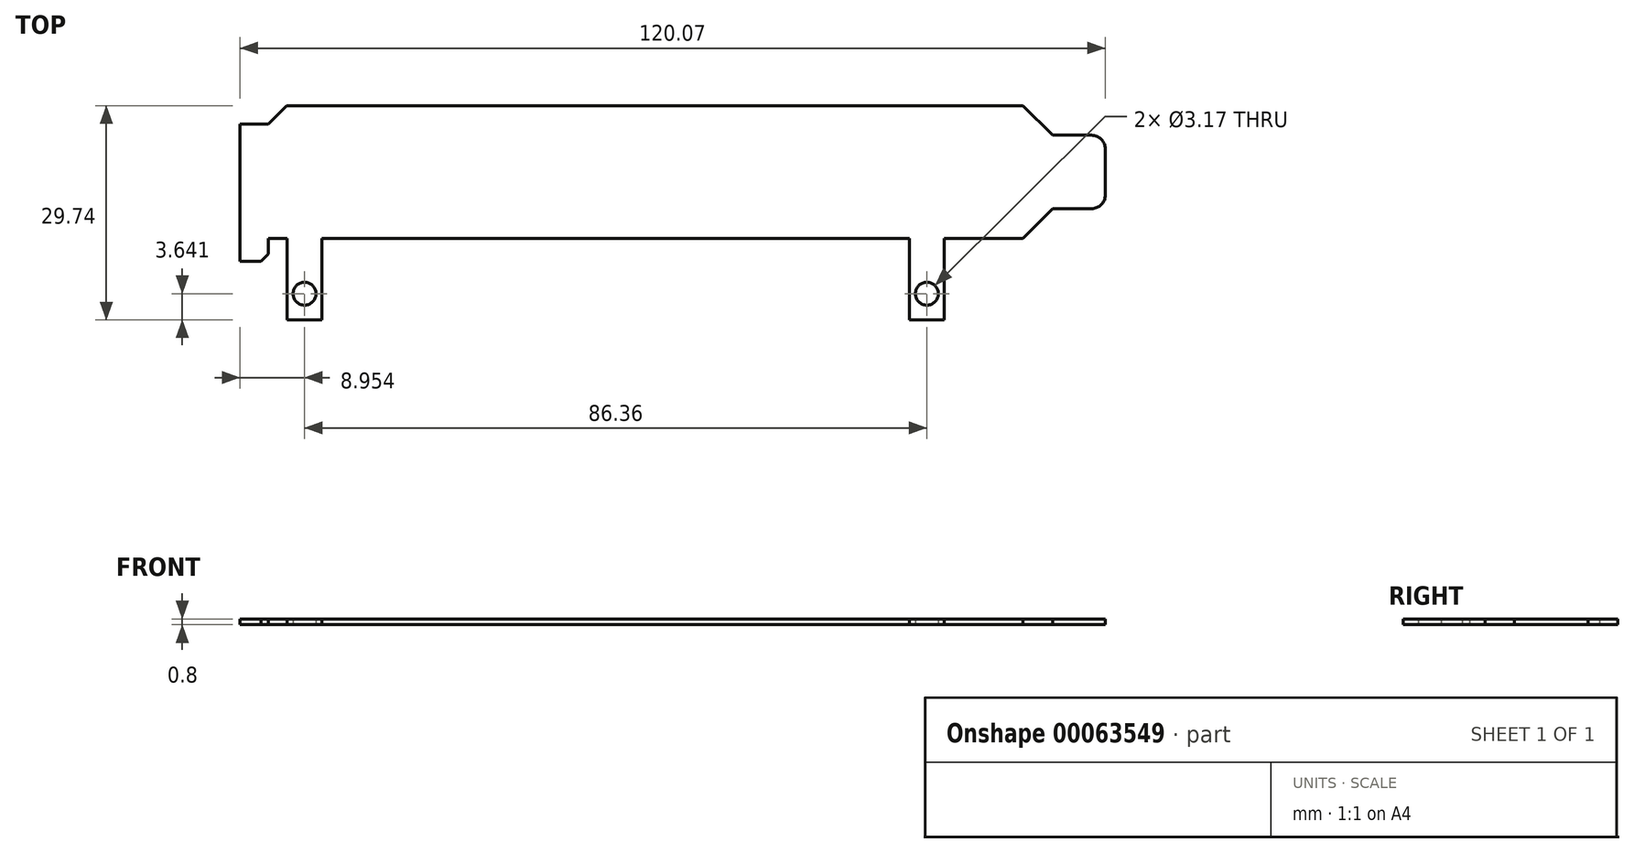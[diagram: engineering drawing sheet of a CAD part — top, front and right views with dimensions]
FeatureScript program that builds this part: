
annotation { "Feature Type Name" : "Feature", "Feature Type Description" : "" }
export const myFeature = defineFeature(function(context is Context, id is Id, definition is map)
    precondition{}
    {
        {
            var Q0;
            Q0=qCreatedBy(makeId("Top.planeOp"),FACE);
            var sketch = newSketch(context, id + "F0", { "sketchPlane" : qUnion([Q0])});
            skLineSegment(sketch, "E0.bottom", {"start": v(0, 0) * mm, "end": v(120.02, 0) * mm, "construction": true});
            skLineSegment(sketch, "E0.top", {"start": v(0, -18.41) * mm, "end": v(120.02, -18.41) * mm, "construction": true});
            skLineSegment(sketch, "E0.left", {"start": v(0, 0) * mm, "end": v(0, -18.41) * mm, "construction": true});
            skLineSegment(sketch, "E1.bottom", {"start": v(118.16, -4.11) * mm, "end": v(112.75, -4.11) * mm});
            skLineSegment(sketch, "E1.top", {"start": v(118.16, -14.3) * mm, "end": v(112.75, -14.3) * mm});
            skLineSegment(sketch, "E1.left", {"start": v(120.07, -6.02) * mm, "end": v(120.07, -12.4) * mm});
            skLineSegment(sketch, "E2", {"start": v(112.75, -4.11) * mm, "end": v(108.64, 0) * mm});
            skLineSegment(sketch, "E3", {"start": v(112.75, -14.3) * mm, "end": v(108.64, -18.41) * mm});
            skPoint(sketch, "E4.visualSharp", {"position": v(120.07, -4.11) * mm});
            skArc(sketch, "E4.filletArc", {"start": v(120.07, -6.02) * mm, "mid": v(119.5, -4.67) * mm, "end": v(118.16, -4.11) * mm});
            skPoint(sketch, "E5.visualSharp", {"position": v(120.07, -14.3) * mm});
            skArc(sketch, "E5.filletArc", {"start": v(118.16, -14.3) * mm, "mid": v(119.5, -13.74) * mm, "end": v(120.07, -12.4) * mm});
            skLineSegment(sketch, "E6", {"start": v(0, -2.54) * mm, "end": v(3.94, -2.54) * mm});
            skLineSegment(sketch, "E7", {"start": v(3.94, -2.54) * mm, "end": v(6.48, 0) * mm});
            skLineSegment(sketch, "E8", {"start": v(0, -18.41) * mm, "end": v(0, -21.59) * mm});
            skLineSegment(sketch, "E9", {"start": v(0, -21.59) * mm, "end": v(2.92, -21.59) * mm});
            skLineSegment(sketch, "E10", {"start": v(2.92, -21.59) * mm, "end": v(3.94, -20.57) * mm});
            skLineSegment(sketch, "E11", {"start": v(3.94, -20.57) * mm, "end": v(3.94, -18.41) * mm});
            skLineSegment(sketch, "E12", {"start": v(6.48, 0) * mm, "end": v(108.64, 0) * mm});
            skLineSegment(sketch, "E13", {"start": v(3.94, -18.41) * mm, "end": v(108.64, -18.41) * mm});
            skLineSegment(sketch, "E14", {"start": v(0, -2.54) * mm, "end": v(0, -18.41) * mm});
            skLineSegment(sketch, "E15", {"start": v(120.02, 0) * mm, "end": v(100.2, 0) * mm, "construction": true});
            skLineSegment(sketch, "E16", {"start": v(120.02, 24.3) * mm, "end": v(100.2, 24.3) * mm, "construction": true});
            skLineSegment(sketch, "E17", {"start": v(100.2, 24.3) * mm, "end": v(96.9, 24.3) * mm, "construction": true});
            skLineSegment(sketch, "E18", {"start": v(96.9, 24.3) * mm, "end": v(93.73, 24.3) * mm, "construction": true});
            skPoint(sketch, "E19.endSnap0", {"position": v(110.1, 0) * mm});
            skPoint(sketch, "E20", {"position": v(95.31, 24.3) * mm});
            skCircle(sketch, "E21", {"center": v(95.31, -26.1) * mm, "radius": 1.59 * mm});
            skLineSegment(sketch, "E22.top", {"start": v(92.91, -29.74) * mm, "end": v(97.71, -29.74) * mm});
            skLineSegment(sketch, "E22.left", {"start": v(92.91, -29.74) * mm, "end": v(92.91, -18.41) * mm});
            skLineSegment(sketch, "E22.right", {"start": v(97.71, -29.74) * mm, "end": v(97.71, -18.41) * mm});
            skPoint(sketch, "E23", {"position": v(95.31, -29.74) * mm});
            skCircle(sketch, "E24.1.0.0", {"center": v(8.95, -26.1) * mm, "radius": 1.59 * mm});
            skLineSegment(sketch, "E24.1.0.1", {"start": v(6.55, -29.74) * mm, "end": v(6.55, -18.41) * mm});
            skPoint(sketch, "E24.1.0.2", {"position": v(8.95, -29.74) * mm});
            skLineSegment(sketch, "E24.1.0.3", {"start": v(11.35, -29.74) * mm, "end": v(11.35, -18.41) * mm});
            skLineSegment(sketch, "E24.1.0.4", {"start": v(6.55, -29.74) * mm, "end": v(11.35, -29.74) * mm});
            skCircle(sketch, "E24.2.0.0", {"center": v(-77.4, -26.1) * mm, "radius": 1.59 * mm});
            skLineSegment(sketch, "E24.2.0.1", {"start": v(-79.8, -29.74) * mm, "end": v(-79.8, -18.41) * mm});
            skPoint(sketch, "E24.2.0.2", {"position": v(-77.4, -29.74) * mm});
            skLineSegment(sketch, "E24.2.0.3", {"start": v(-75, -29.74) * mm, "end": v(-75, -18.41) * mm});
            skLineSegment(sketch, "E24.2.0.4", {"start": v(-79.8, -29.74) * mm, "end": v(-75, -29.74) * mm});
            skLineSegment(sketch, "E24.direction1", {"start": v(92.91, -29.74) * mm, "end": v(6.55, -29.74) * mm, "construction": true});
            skSolve(sketch);
        }
        {
            var Q0;
            Q0=makeQuery(id+"F0.imprint","IMPRINT",FACE,{"disambiguationData":[TD([[makeQuery(id+"F0.imprint","IMPRINT",EDGE,{"derivedFrom":sQuery(id+"F0.wireOp",EDGE,"E1.bottom")}),1.0]])]});
            var Q1;
            Q1=makeQuery(id+"F0.imprint","IMPRINT",FACE,{"disambiguationData":[TD([[makeQuery(id+"F0.imprint","IMPRINT",EDGE,{"derivedFrom":sQuery(id+"F0.wireOp",EDGE,"E24.1.0.0")}),-1.0]])]});
            var Q2;
            Q2=makeQuery(id+"F0.imprint","IMPRINT",FACE,{"disambiguationData":[TD([[makeQuery(id+"F0.imprint","IMPRINT",EDGE,{"derivedFrom":sQuery(id+"F0.wireOp",EDGE,"E21")}),-1.0]])]});
            extrude(context, id + "F1", {"entities" : qUnion([Q0, Q1, Q2]), "depth" : 0.8 * mm});
        }
    });
